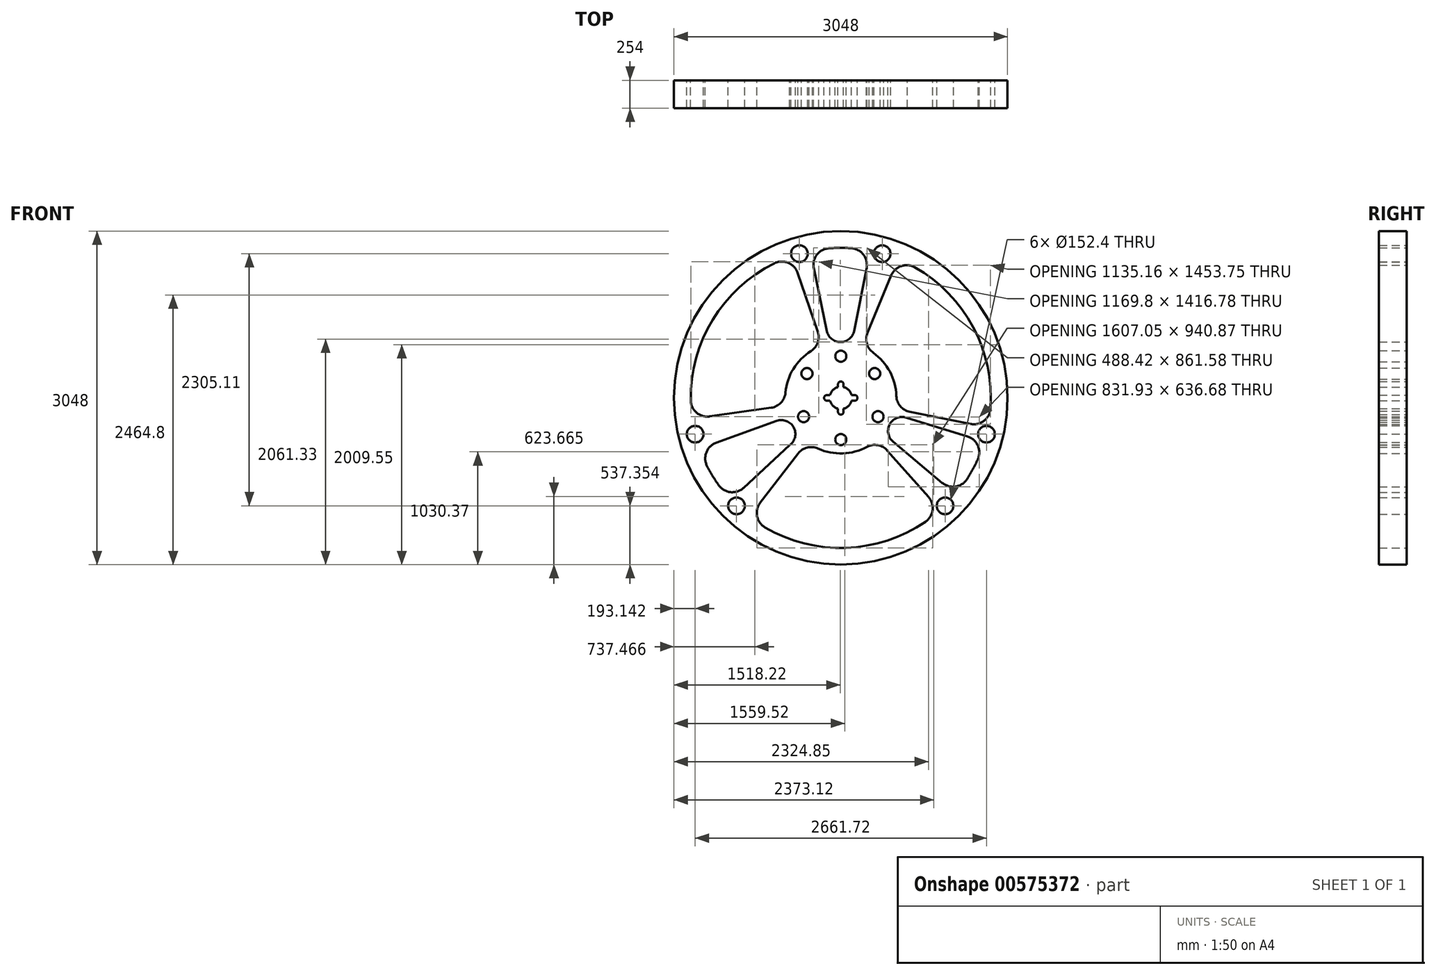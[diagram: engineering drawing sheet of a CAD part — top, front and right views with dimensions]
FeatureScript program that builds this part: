
annotation { "Feature Type Name" : "Feature", "Feature Type Description" : "" }
export const myFeature = defineFeature(function(context is Context, id is Id, definition is map)
    precondition{}
    {
        {
            var Q0;
            Q0=qCreatedBy(makeId("Front.planeOp"),FACE);
            var sketch = newSketch(context, id + "F0", { "sketchPlane" : qUnion([Q0])});
            skCircle(sketch, "E0", {"center": v(0, 0) * mm, "radius": 1524 * mm});
            skArc(sketch, "E1", {"start": v(-1222.32, -622.27) * mm, "mid": v(-1171.98, -712.56) * mm, "end": v(-1115, -798.8) * mm});
            skCircle(sketch, "E2", {"center": v(-378.06, 1318.47) * mm, "radius": 76.2 * mm});
            skCircle(sketch, "E3", {"center": v(378.06, 1318.47) * mm, "radius": 76.2 * mm});
            skCircle(sketch, "E4.1.0", {"center": v(-1330.86, -331.82) * mm, "radius": 76.2 * mm});
            skCircle(sketch, "E4.1.1", {"center": v(-952.8, -986.65) * mm, "radius": 76.2 * mm});
            skCircle(sketch, "E4.2.0", {"center": v(952.8, -986.65) * mm, "radius": 76.2 * mm});
            skCircle(sketch, "E4.2.1", {"center": v(1330.86, -331.82) * mm, "radius": 76.2 * mm});
            skLineSegment(sketch, "E5", {"start": v(-210, 607.29) * mm, "end": v(-395.33, 1143.21) * mm});
            skLineSegment(sketch, "E6", {"start": v(-127.35, 611.1) * mm, "end": v(-246.78, 1184.2) * mm});
            skLineSegment(sketch, "E7", {"start": v(121.55, 612.28) * mm, "end": v(235.54, 1186.48) * mm});
            skLineSegment(sketch, "E8", {"start": v(244.5, 594.24) * mm, "end": v(460.26, 1118.65) * mm});
            skLineSegment(sketch, "E9", {"start": v(629.98, -126.61) * mm, "end": v(1185.92, -238.35) * mm});
            skLineSegment(sketch, "E10", {"start": v(581.67, -177.25) * mm, "end": v(1157.1, -352.6) * mm});
            skLineSegment(sketch, "E11", {"start": v(476.98, -399.49) * mm, "end": v(927.35, -776.7) * mm});
            skLineSegment(sketch, "E12", {"start": v(425.71, -481.32) * mm, "end": v(801.4, -906.08) * mm});
            skLineSegment(sketch, "E13", {"start": v(-391.25, -509.73) * mm, "end": v(-736.52, -959.56) * mm});
            skLineSegment(sketch, "E14", {"start": v(-446.17, -413.15) * mm, "end": v(-887.56, -821.87) * mm});
            skLineSegment(sketch, "E15", {"start": v(-636.2, -90.27) * mm, "end": v(-1197.64, -169.93) * mm});
            skLineSegment(sketch, "E16", {"start": v(-585.4, -210.75) * mm, "end": v(-1138.13, -409.74) * mm});
            skArc(sketch, "E17.trimOffspring", {"start": v(-207.97, -463.48) * mm, "mid": v(17.65, -507.7) * mm, "end": v(239.66, -447.91) * mm});
            skArc(sketch, "E18.trimOffspring", {"start": v(507.7, 17.54) * mm, "mid": v(447.97, 239.55) * mm, "end": v(296.49, 412.5) * mm});
            skArc(sketch, "E19.trimOffspring", {"start": v(-272.34, 428.83) * mm, "mid": v(-433.5, 264.86) * mm, "end": v(-505.86, 46.63) * mm});
            skArc(sketch, "E20.trimOffspring", {"start": v(-692.58, -1183.9) * mm, "mid": v(47.67, -1370.77) * mm, "end": v(773.15, -1132.93) * mm});
            skArc(sketch, "E21.trimOffspring", {"start": v(1153.35, -742.34) * mm, "mid": v(1205.98, -653.37) * mm, "end": v(1251.77, -560.69) * mm});
            skArc(sketch, "E22.trimOffspring", {"start": v(1367.95, -100.06) * mm, "mid": v(1209.52, 646.8) * mm, "end": v(676.34, 1193.25) * mm});
            skArc(sketch, "E23.trimOffspring", {"start": v(96.81, 1368.18) * mm, "mid": v(-6.5, 1371.58) * mm, "end": v(-109.79, 1367.2) * mm});
            skArc(sketch, "E24.trimOffspring", {"start": v(-606.78, 1230.08) * mm, "mid": v(-1170.43, 715.11) * mm, "end": v(-1371.43, -21.42) * mm});
            skPoint(sketch, "E25.visualSharp", {"position": v(-279.83, 1342.75) * mm});
            skArc(sketch, "E25.filletArc", {"start": v(-273.58, 1344.04) * mm, "mid": v(-277.61, 1341.3) * mm, "end": v(-278.53, 1336.52) * mm});
            skArc(sketch, "E26.filletArc", {"start": v(-109.79, 1367.2) * mm, "mid": v(-219.59, 1306.62) * mm, "end": v(-246.78, 1184.2) * mm});
            skArc(sketch, "E27.filletArc", {"start": v(235.54, 1186.48) * mm, "mid": v(207.18, 1308.64) * mm, "end": v(96.81, 1368.18) * mm});
            skPoint(sketch, "E28.visualSharp", {"position": v(-448.26, 1296.28) * mm});
            skArc(sketch, "E28.filletArc", {"start": v(-395.33, 1143.21) * mm, "mid": v(-481.45, 1234.37) * mm, "end": v(-606.78, 1230.08) * mm});
            skPoint(sketch, "E29.visualSharp", {"position": v(-1358, -192.68) * mm});
            skArc(sketch, "E29.filletArc", {"start": v(-1371.43, -21.42) * mm, "mid": v(-1318.06, -134.9) * mm, "end": v(-1197.64, -169.93) * mm});
            skPoint(sketch, "E30.visualSharp", {"position": v(-1290.52, -464.6) * mm});
            skArc(sketch, "E30.filletArc", {"start": v(-1138.13, -409.74) * mm, "mid": v(-1228.2, -497) * mm, "end": v(-1222.32, -622.27) * mm});
            skArc(sketch, "E31.filletArc", {"start": v(-1115, -798.8) * mm, "mid": v(-1006.48, -861.67) * mm, "end": v(-887.56, -821.87) * mm});
            skPoint(sketch, "E32.visualSharp", {"position": v(-835.14, -1088.04) * mm});
            skArc(sketch, "E32.filletArc", {"start": v(-736.52, -959.56) * mm, "mid": v(-765.19, -1081.65) * mm, "end": v(-692.58, -1183.9) * mm});
            skPoint(sketch, "E33.visualSharp", {"position": v(908.7, -1027.4) * mm});
            skArc(sketch, "E33.filletArc", {"start": v(773.15, -1132.93) * mm, "mid": v(838.47, -1025.88) * mm, "end": v(801.4, -906.08) * mm});
            skPoint(sketch, "E34.visualSharp", {"position": v(1051.51, -880.69) * mm});
            skArc(sketch, "E34.filletArc", {"start": v(927.35, -776.7) * mm, "mid": v(1048.1, -810.53) * mm, "end": v(1153.35, -742.34) * mm});
            skPoint(sketch, "E35.visualSharp", {"position": v(1312.03, -399.82) * mm});
            skArc(sketch, "E35.filletArc", {"start": v(1251.77, -560.69) * mm, "mid": v(1251.4, -435.28) * mm, "end": v(1157.1, -352.6) * mm});
            skPoint(sketch, "E36.visualSharp", {"position": v(1344.7, -270.26) * mm});
            skArc(sketch, "E36.filletArc", {"start": v(1185.92, -238.35) * mm, "mid": v(1308.15, -210.29) * mm, "end": v(1367.95, -100.06) * mm});
            skPoint(sketch, "E37.visualSharp", {"position": v(521.88, 1268.43) * mm});
            skArc(sketch, "E37.filletArc", {"start": v(676.34, 1193.25) * mm, "mid": v(551.46, 1204.72) * mm, "end": v(460.26, 1118.65) * mm});
            skArc(sketch, "E38", {"start": v(-98.37, -25.4) * mm, "mid": v(-71.84, -71.84) * mm, "end": v(-25.4, -98.37) * mm});
            skCircle(sketch, "E39", {"center": v(0, 381) * mm, "radius": 50.8 * mm});
            skCircle(sketch, "E40", {"center": v(0, -381) * mm, "radius": 50.8 * mm});
            skCircle(sketch, "E41", {"center": v(-309.31, 222.46) * mm, "radius": 50.8 * mm});
            skCircle(sketch, "E42", {"center": v(309.31, 222.46) * mm, "radius": 50.8 * mm});
            skCircle(sketch, "E43", {"center": v(339.93, -172.07) * mm, "radius": 50.8 * mm});
            skCircle(sketch, "E44", {"center": v(-339.93, -172.07) * mm, "radius": 50.8 * mm});
            skArc(sketch, "E45", {"start": v(25.4, 124.5) * mm, "mid": v(0, 149.9) * mm, "end": v(-25.4, 124.5) * mm});
            skArc(sketch, "E46", {"start": v(-127, 25.4) * mm, "mid": v(-152.4, 0) * mm, "end": v(-127, -25.4) * mm});
            skArc(sketch, "E47", {"start": v(-25.4, -127) * mm, "mid": v(0, -152.4) * mm, "end": v(25.4, -127) * mm});
            skArc(sketch, "E48", {"start": v(127, -25.4) * mm, "mid": v(152.4, 0) * mm, "end": v(127, 25.4) * mm});
            skLineSegment(sketch, "E49", {"start": v(-25.4, 124.5) * mm, "end": v(-25.4, 98.37) * mm});
            skLineSegment(sketch, "E50", {"start": v(25.4, 124.5) * mm, "end": v(25.4, 98.37) * mm});
            skLineSegment(sketch, "E51", {"start": v(127, 25.4) * mm, "end": v(98.37, 25.4) * mm});
            skLineSegment(sketch, "E52", {"start": v(127, -25.4) * mm, "end": v(98.37, -25.4) * mm});
            skLineSegment(sketch, "E53", {"start": v(25.4, -127) * mm, "end": v(25.4, -98.37) * mm});
            skLineSegment(sketch, "E54", {"start": v(-25.4, -127) * mm, "end": v(-25.4, -98.37) * mm});
            skLineSegment(sketch, "E55", {"start": v(-127, -25.4) * mm, "end": v(-98.37, -25.4) * mm});
            skLineSegment(sketch, "E56", {"start": v(-127, 25.4) * mm, "end": v(-98.37, 25.4) * mm});
            skArc(sketch, "E57.trimOffspring", {"start": v(-25.4, 98.37) * mm, "mid": v(-71.84, 71.84) * mm, "end": v(-98.37, 25.4) * mm});
            skArc(sketch, "E58.trimOffspring", {"start": v(98.37, 25.4) * mm, "mid": v(71.84, 71.84) * mm, "end": v(25.4, 98.37) * mm});
            skArc(sketch, "E59.trimOffspring", {"start": v(25.4, -98.37) * mm, "mid": v(71.84, -71.84) * mm, "end": v(98.37, -25.4) * mm});
            skPoint(sketch, "E60.visualSharp", {"position": v(193.29, 469.8) * mm});
            skArc(sketch, "E60.filletArc", {"start": v(244.5, 594.24) * mm, "mid": v(238.9, 494.34) * mm, "end": v(296.49, 412.5) * mm});
            skPoint(sketch, "E61.visualSharp", {"position": v(498.04, -100.1) * mm});
            skArc(sketch, "E61.filletArc", {"start": v(507.7, 17.54) * mm, "mid": v(543.79, -75.79) * mm, "end": v(629.98, -126.61) * mm});
            skPoint(sketch, "E62.visualSharp", {"position": v(-166.02, 480.1) * mm});
            skArc(sketch, "E62.filletArc", {"start": v(-272.34, 428.83) * mm, "mid": v(-210.16, 507.23) * mm, "end": v(-210, 607.29) * mm});
            skPoint(sketch, "E63.visualSharp", {"position": v(-502.96, -71.36) * mm});
            skArc(sketch, "E63.filletArc", {"start": v(-636.2, -90.27) * mm, "mid": v(-547.24, -44.47) * mm, "end": v(-505.86, 46.63) * mm});
            skPoint(sketch, "E64.visualSharp", {"position": v(-309.31, -402.98) * mm});
            skArc(sketch, "E64.filletArc", {"start": v(-207.97, -463.48) * mm, "mid": v(-307.65, -454.76) * mm, "end": v(-391.25, -509.73) * mm});
            skPoint(sketch, "E65.visualSharp", {"position": v(336.56, -380.52) * mm});
            skArc(sketch, "E65.filletArc", {"start": v(425.71, -481.32) * mm, "mid": v(338.5, -432.29) * mm, "end": v(239.66, -447.91) * mm});
            skCircle(sketch, "E66", {"center": v(0, 0) * mm, "radius": 444.5 * mm});
            skArc(sketch, "E67", {"start": v(-127.35, 611.1) * mm, "mid": v(-2.42, 510) * mm, "end": v(121.55, 612.28) * mm});
            skPoint(sketch, "E68.start.orphan", {"position": v(0, 508) * mm});
            skArc(sketch, "E69", {"start": v(608.94, -185.56) * mm, "mid": v(450.43, -235.45) * mm, "end": v(476.98, -399.49) * mm});
            skArc(sketch, "E70", {"start": v(-467.1, -432.52) * mm, "mid": v(-430.32, -270.47) * mm, "end": v(-585.4, -210.75) * mm});
            skSolve(sketch);
        }
        {
            var Q0;
            Q0 = qSketchRegion(id + "F0", true);
            var Q1;
            Q1=makeQuery(id+"F0.imprint","IMPRINT",FACE,{"disambiguationData":[TD([[makeQuery(id+"F0.imprint","IMPRINT",EDGE,{"derivedFrom":sQuery(id+"F0.wireOp",EDGE,"E38")}),-1.0]])]});
            extrude(context, id + "F1", {"entities" : qUnion([Q0, Q1]), "depth" : 254 * mm, "offsetDistance" : 25.4 * mm});
        }
    });
